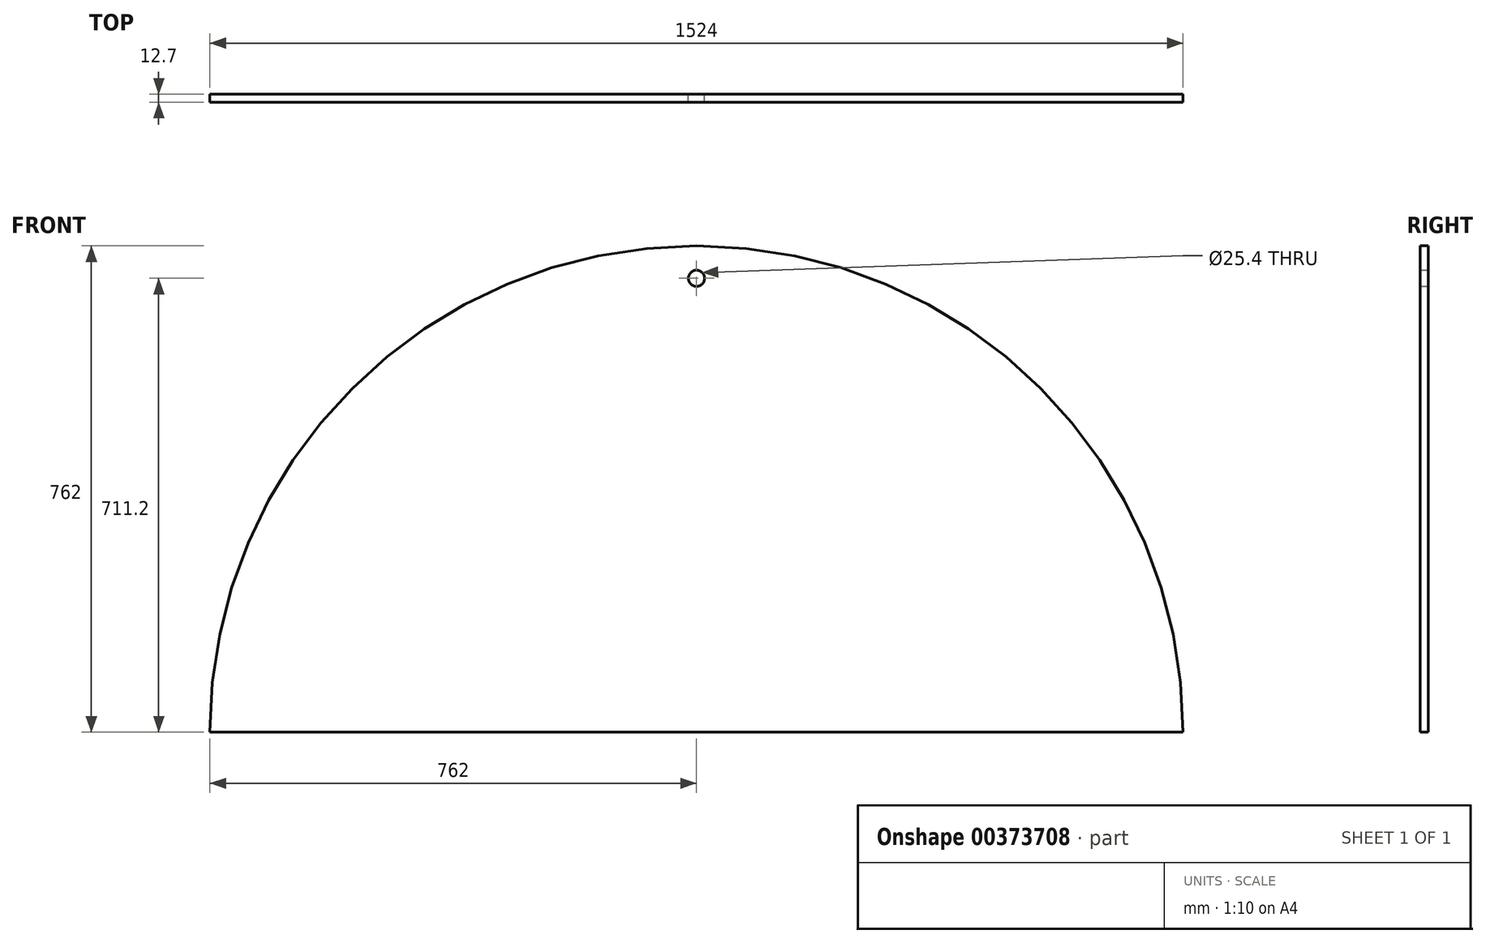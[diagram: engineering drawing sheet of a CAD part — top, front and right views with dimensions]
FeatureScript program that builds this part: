
annotation { "Feature Type Name" : "Feature", "Feature Type Description" : "" }
export const myFeature = defineFeature(function(context is Context, id is Id, definition is map)
    precondition{}
    {
        {
            var Q0;
            Q0=qCreatedBy(makeId("Front.planeOp"),FACE);
            var sketch = newSketch(context, id + "F0", { "sketchPlane" : qUnion([Q0])});
            skArc(sketch, "E0", {"start": v(762, 0) * mm, "mid": v(0, 762) * mm, "end": v(-762, 0) * mm});
            skLineSegment(sketch, "E1", {"start": v(-762, 0) * mm, "end": v(762, 0) * mm});
            skLineSegment(sketch, "E2", {"start": v(0, 0) * mm, "end": v(0, 762) * mm, "construction": true});
            skCircle(sketch, "E3", {"center": v(0, 711.2) * mm, "radius": 12.7 * mm});
            skSolve(sketch);
        }
        {
            var Q0;
            Q0 = qSketchRegion(id + "F0", true);
            extrude(context, id + "F1", {"entities" : qUnion([Q0]), "endBound" : BoundingType.SYMMETRIC, "depth" : 12.7 * mm});
        }
    });
